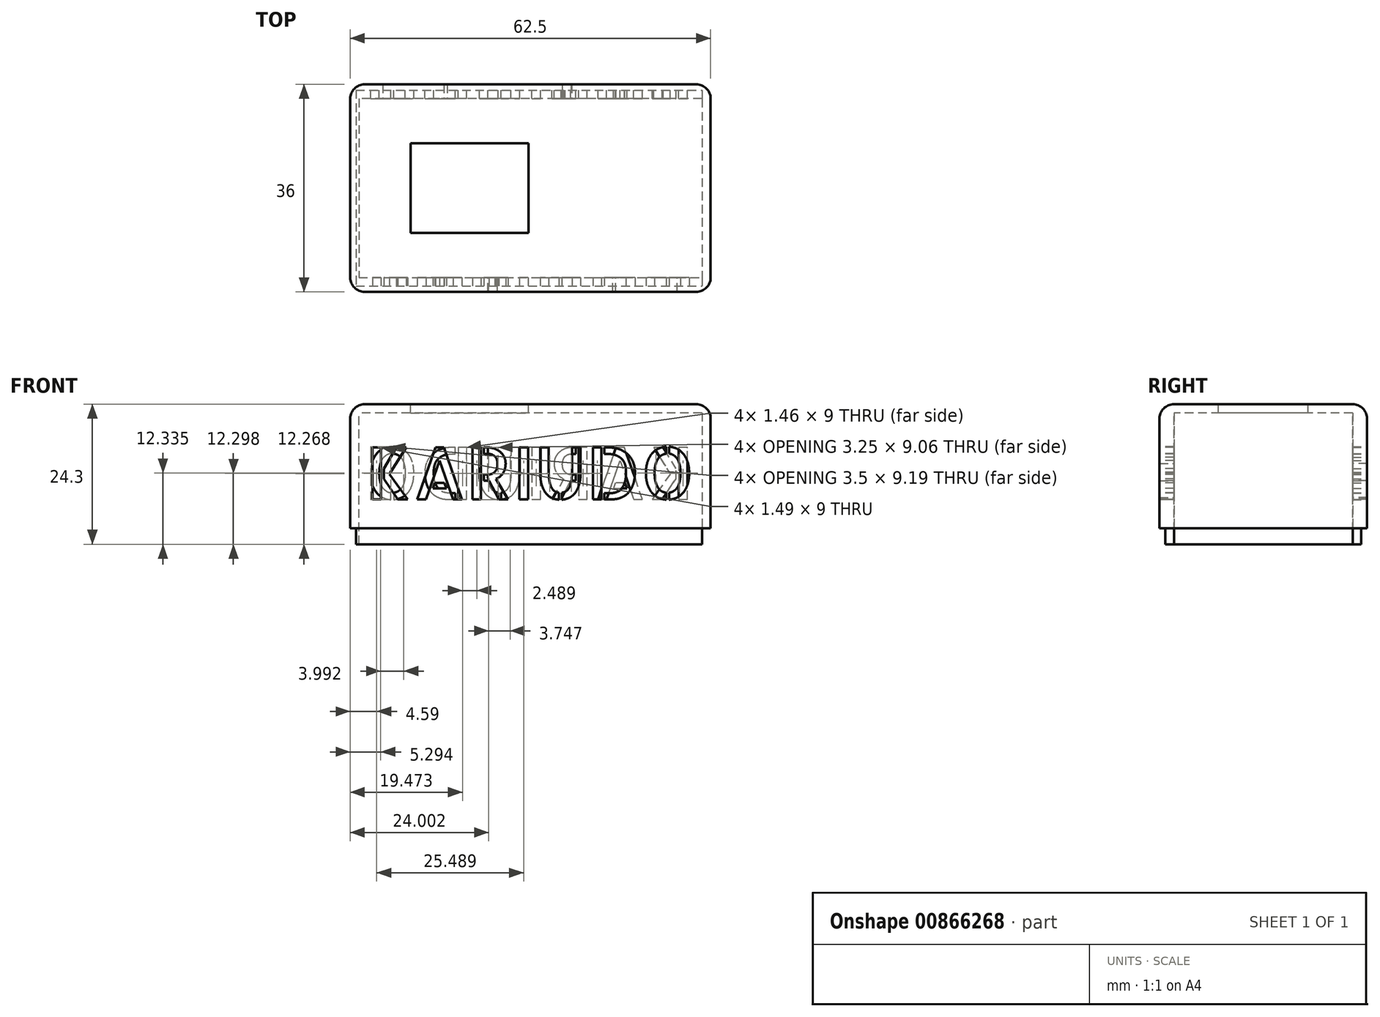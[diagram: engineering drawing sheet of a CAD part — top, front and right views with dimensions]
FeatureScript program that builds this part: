
annotation { "Feature Type Name" : "Feature", "Feature Type Description" : "" }
export const myFeature = defineFeature(function(context is Context, id is Id, definition is map)
    precondition{}
    {
        {
            var Q0;
            Q0=qCreatedBy(makeId("Top.planeOp"),FACE);
            var sketch = newSketch(context, id + "F0", { "sketchPlane" : qUnion([Q0])});
            skLineSegment(sketch, "E0.bottom", {"start": v(-31.16, 18) * mm, "end": v(31.34, 18) * mm});
            skLineSegment(sketch, "E0.top", {"start": v(-31.16, -18) * mm, "end": v(31.34, -18) * mm});
            skLineSegment(sketch, "E0.left", {"start": v(-31.16, 18) * mm, "end": v(-31.16, -18) * mm});
            skLineSegment(sketch, "E0.right", {"start": v(31.34, 18) * mm, "end": v(31.34, -18) * mm});
            skLineSegment(sketch, "E1.bottom", {"start": v(-30.16, 17) * mm, "end": v(29.84, 17) * mm});
            skLineSegment(sketch, "E1.top", {"start": v(-30.16, -17) * mm, "end": v(29.84, -17) * mm});
            skLineSegment(sketch, "E1.left", {"start": v(-30.16, 17) * mm, "end": v(-30.16, -17) * mm});
            skLineSegment(sketch, "E1.right", {"start": v(29.84, 17) * mm, "end": v(29.84, -17) * mm});
            skLineSegment(sketch, "E2", {"start": v(29.84, 15.5) * mm, "end": v(-28.66, 15.5) * mm});
            skLineSegment(sketch, "E3", {"start": v(-28.66, 15.5) * mm, "end": v(-28.66, -15.5) * mm});
            skLineSegment(sketch, "E4", {"start": v(-28.66, -15.5) * mm, "end": v(29.84, -15.5) * mm});
            skSolve(sketch);
        }
        {
            var Q0;
            {var subQ1=sQuery(id+"F0.wireOp",EDGE,"E1.bottom");Q0=makeQuery(id+"F0.imprint","IMPRINT",FACE,{"disambiguationData":[TD([[makeQuery(id+"F0.imprint","IMPRINT",EDGE,{"derivedFrom":subQ1}),-1.0]])]});}
            extrude(context, id + "F1", {"entities" : qUnion([Q0]), "oppositeDirection" : true, "depth" : 2.8 * mm});
        }
        {
            var Q0;
            Q0=makeQuery(id+"F0.imprint","IMPRINT",FACE,{"disambiguationData":[TD([[makeQuery(id+"F0.imprint","IMPRINT",EDGE,{"derivedFrom":sQuery(id+"F0.wireOp",EDGE,"E0.bottom")}),-1.0]])]});
            var Q1;
            {var subQ1=sQuery(id+"F0.wireOp",EDGE,"E1.bottom");Q1=makeQuery(id+"F0.imprint","IMPRINT",FACE,{"disambiguationData":[TD([[makeQuery(id+"F0.imprint","IMPRINT",EDGE,{"derivedFrom":subQ1}),-1.0]])]});}
            extrude(context, id + "F2", {"entities" : qUnion([Q0, Q1]), "operationType" : NewBodyOperationType.ADD, "depth" : 20 * mm});
        }
        {
            var Q0;
            Q0=makeQuery(id+"F2.opExtrude","SWEPT_FACE",FACE,{"disambiguationData":[OSD([sQuery(id+"F0.wireOp",EDGE,"E0.right")])]});
            var sketch = newSketch(context, id + "F3", { "sketchPlane" : qUnion([Q0])});
            skLineSegment(sketch, "E5.bottom", {"start": v(-18, 20) * mm, "end": v(18, 20) * mm});
            skLineSegment(sketch, "E5.top", {"start": v(-18, 21.5) * mm, "end": v(18, 21.5) * mm});
            skLineSegment(sketch, "E5.left", {"start": v(-18, 20) * mm, "end": v(-18, 21.5) * mm});
            skLineSegment(sketch, "E5.right", {"start": v(18, 20) * mm, "end": v(18, 21.5) * mm});
            skSolve(sketch);
        }
        {
            var Q0;
            Q0=makeQuery(id+"F3.imprint","IMPRINT",FACE,{"disambiguationData":[TD([[makeQuery(id+"F3.imprint","IMPRINT",EDGE,{"derivedFrom":sQuery(id+"F3.wireOp",EDGE,"E5.bottom")}),-1.0]])]});
            var Q1;
            Q1=qSketchRegion(id+"FGHyg4ucGbV6FiT_1",true);
            var Q2;
            Q2=makeQuery(id+"F2.opExtrude","SWEPT_FACE",FACE,{"disambiguationData":[OSD([sQuery(id+"F0.wireOp",EDGE,"E0.left")])]});
            extrude(context, id + "F4", {"entities" : qUnion([Q0, Q1]), "operationType" : NewBodyOperationType.ADD, "endBound" : BoundingType.UP_TO_SURFACE, "oppositeDirection" : true, "endBoundEntityFace" : qUnion([Q2]), "depth" : 62.3 * mm});
        }
        {
            var Q0;
            Q0=makeQuery(id+"F4.opExtrude","CAP_EDGE",EDGE,{"disambiguationData":[OSD([sQuery(id+"F3.wireOp",EDGE,"E5.top")])],"isStart":true});
            var Q1;
            Q1=makeQuery(id+"F4.opExtrude","SWEPT_EDGE",EDGE,{"disambiguationData":[OSD([sQuery(id+"F3.wireOp",EDGE,"E5.top"),sQuery(id+"F3.wireOp",EDGE,"E5.left")])]});
            var Q2;
            Q2=makeQuery(id+"F4.boolean.opBoolean","MERGE",EDGE,{"derivedFrom":[makeQuery(id+"F2.opExtrude","SWEPT_EDGE",EDGE,{"disambiguationData":[OSD([sQuery(id+"F0.wireOp",EDGE,"E0.top"),sQuery(id+"F0.wireOp",EDGE,"E0.right")])]}),makeQuery(id+"F4.opExtrude","CAP_EDGE",EDGE,{"disambiguationData":[OSD([sQuery(id+"F3.wireOp",EDGE,"E5.left")])],"isStart":true})]});
            var Q3;
            Q3=makeQuery(id+"F4.boolean.opBoolean","MERGE",EDGE,{"derivedFrom":[makeQuery(id+"F2.opExtrude","SWEPT_EDGE",EDGE,{"disambiguationData":[OSD([sQuery(id+"F0.wireOp",EDGE,"E0.bottom"),sQuery(id+"F0.wireOp",EDGE,"E0.right")])]}),makeQuery(id+"F4.opExtrude","CAP_EDGE",EDGE,{"disambiguationData":[OSD([sQuery(id+"F3.wireOp",EDGE,"E5.right")])],"isStart":true})]});
            var Q4;
            Q4=makeQuery(id+"F4.opExtrude","SWEPT_EDGE",EDGE,{"disambiguationData":[OSD([sQuery(id+"F3.wireOp",EDGE,"E5.top"),sQuery(id+"F3.wireOp",EDGE,"E5.right")])]});
            var Q5;
            Q5=makeQuery(id+"F4.boolean.opBoolean","MERGE",EDGE,{"derivedFrom":[makeQuery(id+"F2.opExtrude","SWEPT_EDGE",EDGE,{"disambiguationData":[OSD([sQuery(id+"F0.wireOp",EDGE,"E0.bottom"),sQuery(id+"F0.wireOp",EDGE,"E0.left")])]}),makeQuery(id+"F4.opExtrude","CAP_EDGE",EDGE,{"disambiguationData":[OSD([sQuery(id+"F3.wireOp",EDGE,"E5.right")])],"isStart":false})]});
            var Q6;
            Q6=makeQuery(id+"F4.opExtrude","CAP_EDGE",EDGE,{"disambiguationData":[OSD([sQuery(id+"F3.wireOp",EDGE,"E5.top")])],"isStart":false});
            var Q7;
            Q7=makeQuery(id+"F4.boolean.opBoolean","MERGE",EDGE,{"derivedFrom":[makeQuery(id+"F2.opExtrude","SWEPT_EDGE",EDGE,{"disambiguationData":[OSD([sQuery(id+"F0.wireOp",EDGE,"E0.top"),sQuery(id+"F0.wireOp",EDGE,"E0.left")])]}),makeQuery(id+"F4.opExtrude","CAP_EDGE",EDGE,{"disambiguationData":[OSD([sQuery(id+"F3.wireOp",EDGE,"E5.left")])],"isStart":false})]});
            fillet(context, id + "F5", {"entities" : qUnion([Q0, Q1, Q2, Q3, Q4, Q5, Q6, Q7]), "radius" : 2.5 * mm, "tangentPropagation" : true, "allowEdgeOverflow" : false});
        }
        {
            var Q0;
            {var subQ0=sQuery(id+"F0.wireOp",EDGE,"E3");Q0=makeQuery(id+"FEPfuos01jypXZx_1.boolean.opBoolean","SPLIT",FACE,{"disambiguationData":[TD([makeQuery(id+"FEPfuos01jypXZx_1.opExtrude","SWEPT_FACE",FACE,{"disambiguationData":[OSD([sQuery(id+"FNJi3SJlg6xjIKS_1.wireOp",EDGE,"CGCuMa7v-HkjL-wQTo-F6Tt-e60EdCvoSJhP.bottom")])]})])],"derivedFrom":makeQuery(id+"F2.boolean.opBoolean","MERGE",FACE,{"derivedFrom":[makeQuery(id+"F1.opExtrude","SWEPT_FACE",FACE,{"disambiguationData":[OSD([subQ0])]}),makeQuery(id+"F2.opExtrude","SWEPT_FACE",FACE,{"disambiguationData":[OSD([subQ0])]})]})});}
            extrude(context, id + "F6", {"entities" : qUnion([Q0]), "operationType" : NewBodyOperationType.REMOVE, "oppositeDirection" : true, "depth" : 1 * mm});
        }
        {
            var Q0;
            Q0=makeQuery(id+"F4.boolean.opBoolean","MERGE",FACE,{"derivedFrom":[makeQuery(id+"F2.opExtrude","SWEPT_FACE",FACE,{"disambiguationData":[OSD([sQuery(id+"F0.wireOp",EDGE,"E0.top")])]}),makeQuery(id+"F4.opExtrude","SWEPT_FACE",FACE,{"disambiguationData":[OSD([sQuery(id+"F3.wireOp",EDGE,"E5.left")])]})]});
            var sketch = newSketch(context, id + "F7", { "sketchPlane" : qUnion([Q0])});
            skText(sketch, "E6", { "text": "KARIUDO", "fontName": "AllertaStencil-Regular.ttf"});
            const initialGuessF7  = {"E6": [-0.02845, 0.005, 1, 0, 0.009]};
            skSetInitialGuess(sketch, initialGuessF7);
            skSolve(sketch);
        }
        {
            var Q0;
            Q0=qSketchRegion(id+"F7",true);
            extrude(context, id + "F8", {"entities" : qUnion([Q0]), "operationType" : NewBodyOperationType.REMOVE, "oppositeDirection" : true, "offsetDistance" : 25 * mm, "depth" : 4 * mm});
        }
        {
            var Q0;
            Q0=makeQuery(id+"F4.boolean.opBoolean","MERGE",FACE,{"derivedFrom":[makeQuery(id+"F2.opExtrude","SWEPT_FACE",FACE,{"disambiguationData":[OSD([sQuery(id+"F0.wireOp",EDGE,"E0.bottom")])]}),makeQuery(id+"F4.opExtrude","SWEPT_FACE",FACE,{"disambiguationData":[OSD([sQuery(id+"F3.wireOp",EDGE,"E5.right")])]})]});
            var sketch = newSketch(context, id + "F9", { "sketchPlane" : qUnion([Q0])});
            skText(sketch, "E7", { "text": "KARIUDO", "fontName": "AllertaStencil-Regular.ttf"});
            const initialGuessF9  = {"E7": [-0.02845, 0.005, 1, 0, 0.009]};
            skSetInitialGuess(sketch, initialGuessF9);
            skSolve(sketch);
        }
        {
            var Q0;
            Q0=qSketchRegion(id+"F9",true);
            extrude(context, id + "F10", {"entities" : qUnion([Q0]), "operationType" : NewBodyOperationType.REMOVE, "oppositeDirection" : true, "offsetDistance" : 25 * mm, "depth" : 4 * mm});
        }
        {
            var Q0;
            Q0=makeQuery(id+"F4.opExtrude","SWEPT_FACE",FACE,{"disambiguationData":[OSD([sQuery(id+"F3.wireOp",EDGE,"E5.top")])]});
            var sketch = newSketch(context, id + "F11", { "sketchPlane" : qUnion([Q0])});
            skLineSegment(sketch, "E8.bottom", {"start": v(-20.66, 7.8) * mm, "end": v(-0.26, 7.8) * mm});
            skLineSegment(sketch, "E8.top", {"start": v(-20.66, -7.8) * mm, "end": v(-0.26, -7.8) * mm});
            skLineSegment(sketch, "E8.left", {"start": v(-20.66, 7.8) * mm, "end": v(-20.66, -7.8) * mm});
            skLineSegment(sketch, "E8.right", {"start": v(-0.26, 7.8) * mm, "end": v(-0.26, -7.8) * mm});
            skSolve(sketch);
        }
        {
            var Q0;
            Q0=makeQuery(id+"F11.imprint","IMPRINT",FACE,{"disambiguationData":[TD([[makeQuery(id+"F11.imprint","IMPRINT",EDGE,{"derivedFrom":sQuery(id+"F11.wireOp",EDGE,"E8.bottom")}),-1.0]])]});
            extrude(context, id + "F12", {"entities" : qUnion([Q0]), "operationType" : NewBodyOperationType.REMOVE, "endBound" : BoundingType.THROUGH_ALL, "oppositeDirection" : true, "depth" : 2 * mm, "offsetDistance" : 25 * mm});
        }
    });
